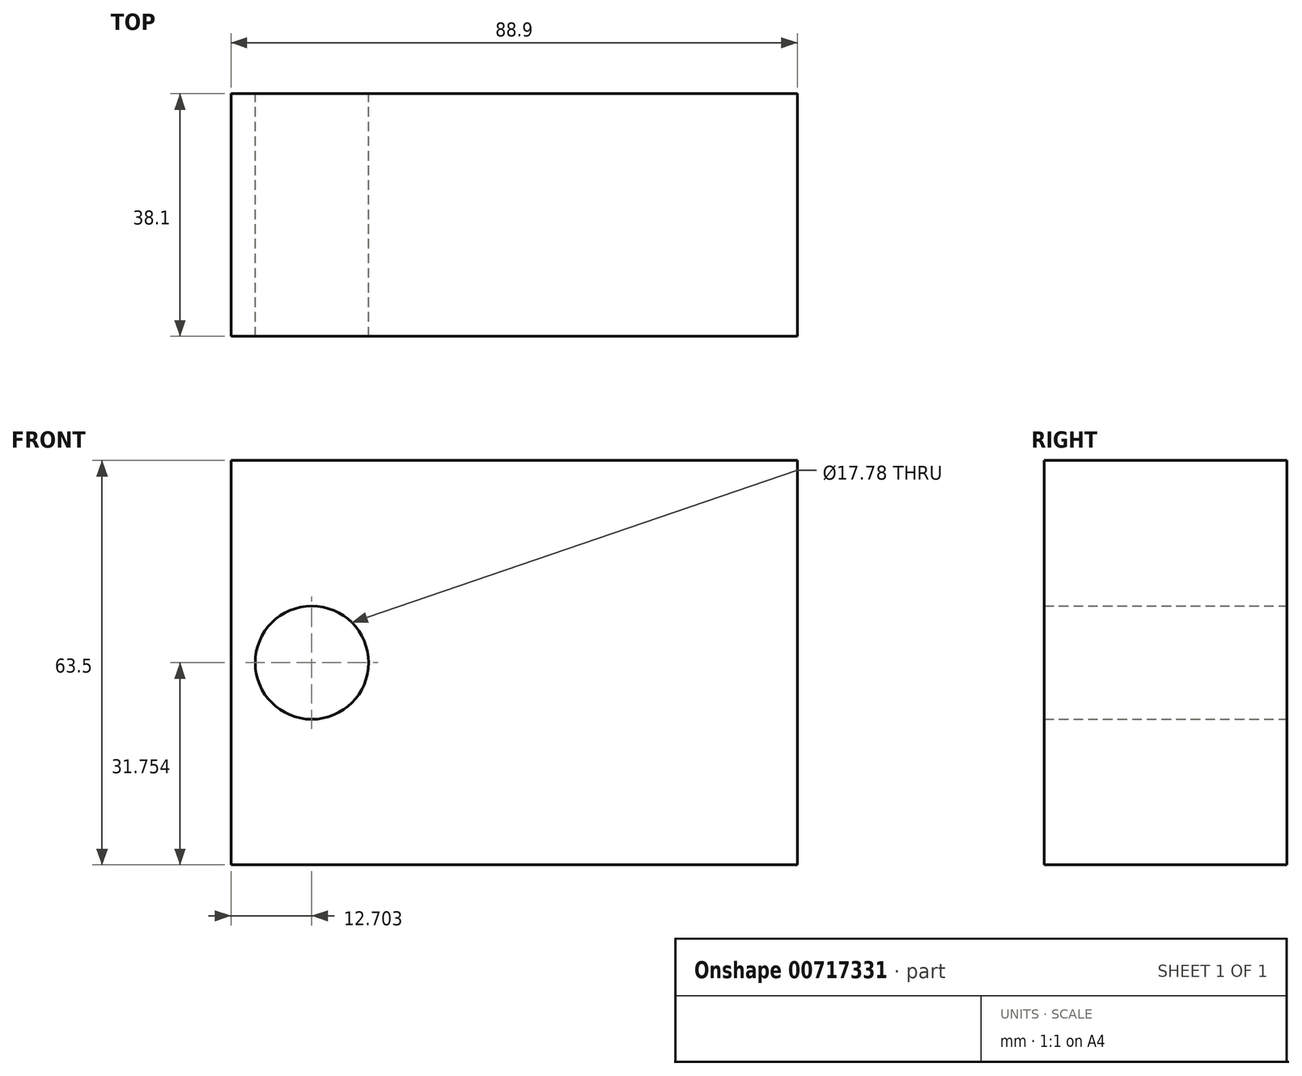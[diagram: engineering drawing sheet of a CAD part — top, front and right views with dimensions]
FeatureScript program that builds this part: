
annotation { "Feature Type Name" : "Feature", "Feature Type Description" : "" }
export const myFeature = defineFeature(function(context is Context, id is Id, definition is map)
    precondition{}
    {
        {
            var Q0;
            Q0=qCreatedBy(makeId("Front.planeOp"),FACE);
            var sketch = newSketch(context, id + "F0", { "sketchPlane" : qUnion([Q0])});
            skLineSegment(sketch, "E0.bottom", {"start": v(-38.23, 28.68) * mm, "end": v(50.67, 28.68) * mm});
            skLineSegment(sketch, "E0.top", {"start": v(-38.23, -34.82) * mm, "end": v(50.67, -34.82) * mm});
            skLineSegment(sketch, "E0.left", {"start": v(-38.23, 28.68) * mm, "end": v(-38.23, -34.82) * mm});
            skLineSegment(sketch, "E0.right", {"start": v(50.67, 28.68) * mm, "end": v(50.67, -34.82) * mm});
            skCircle(sketch, "E1", {"center": v(-25.53, -3.07) * mm, "radius": 8.9 * mm});
            skSolve(sketch);
        }
        {
            var Q0;
            Q0 = qSketchRegion(id + "F0", true);
            extrude(context, id + "F1", {"entities" : qUnion([Q0]), "depth" : 38.1 * mm, "offsetDistance" : 25.4 * mm});
        }
    });
